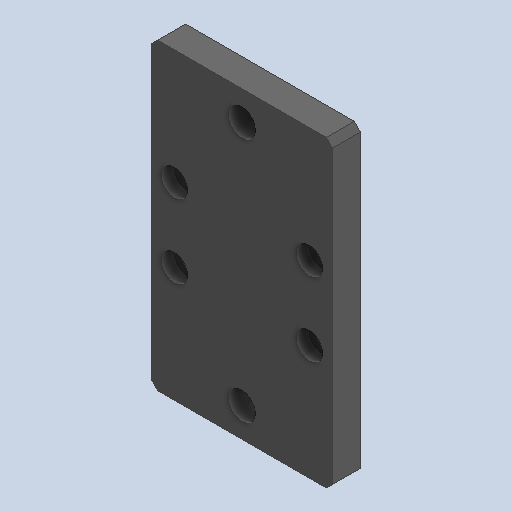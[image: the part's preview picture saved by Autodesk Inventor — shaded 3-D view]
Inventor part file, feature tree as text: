
AUTODESK INVENTOR PART (.ipt)
format: ipt  version: 2024.2 (Build 282272000, 272)  size: 183,296 bytes
history: native  units: in
note: dims shown in document units (in); Inventor stores cm internally (conversion verified against a paired STEP export)
features: hole x3, extrude x2, chamfer x1
ambient origin geometry x8: Origin, YZ Plane, XZ Plane, XY Plane, X Axis, Y Axis, Z Axis, Center Point
bodies: Solid1 (feature_tree)
feature tree (6):
  extrude  "Extrusion1"  Depth=0.1791in TaperAngle=0.0deg
  extrude  "Extrusion2"  Depth=0.8661in
  hole  "Hole1"  [1 undecoded]
  hole  "Hole3"  [1 undecoded]
  hole  "Hole6"  [1 undecoded]
  chamfer  "Chamfer3"  [1 undecoded]
note: 4 required parameter values undecoded (feature->parameter linkage not recoverable at this tier; creation-order binding heuristic only, values carry confidence <= 0.55)
